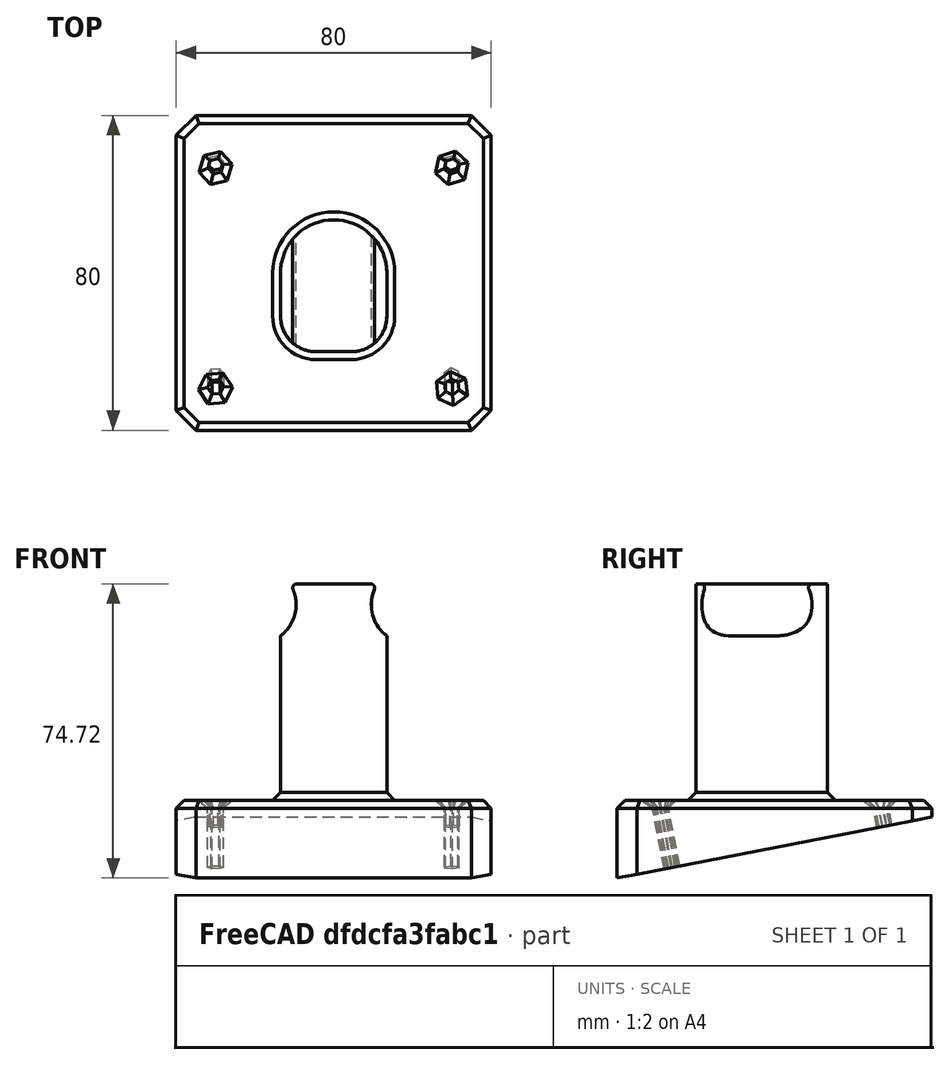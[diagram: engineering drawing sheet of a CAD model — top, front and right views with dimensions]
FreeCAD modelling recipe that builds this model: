
FCSTD DOCUMENT  (FreeCAD 0.19R)
Label: ryobiholder.stl
License: All rights reserved
LicenseURL: http://en.wikipedia.org/wiki/All_rights_reserved
objects: Sketcher::SketchObject×6, PartDesign::Pocket×3, PartDesign::Pad×2, PartDesign::Fillet×2, PartDesign::Chamfer×2, PartDesign::Body×1, Mesh::Feature×1
note: 25 computed .brp shape members not serialized (recipe doc carries the construction recipe); baked Part::Feature solids carry a one-line shape summary decoded from their .brp

FEATURE [Sketcher::SketchObject] Sketch
  FullyConstrained = true
  MapMode = 5
  Support = -> [XY_Plane]
  sketch-geometry (4):
    g0: LineSegment StartX=-40 StartY=40 StartZ=0 EndX=40 EndY=40 EndZ=0
    g1: LineSegment StartX=40 StartY=40 StartZ=0 EndX=40 EndY=-40 EndZ=0
    g2: LineSegment StartX=40 StartY=-40 StartZ=0 EndX=-40 EndY=-40 EndZ=0
    g3: LineSegment StartX=-40 StartY=-40 StartZ=0 EndX=-40 EndY=40 EndZ=0
  constraints (11):
    c: Coincident(g0,g1)
    c: Coincident(g1,g2)
    c: Coincident(g2,g3)
    c: Coincident(g3,g0)
    c: Horizontal(g0)
    c: Horizontal(g2)
    c: Vertical(g1)
    c: Vertical(g3)
    c: Symmetric(g1,g0,g-1)
    c: Equal(g3,g0)
    c: Distance(g0) = 80
FEATURE [PartDesign::Pad] Pad
  Direction = (1,1,1)
  Length = 20
  Length2 = 100
  Profile = -> Sketch
  Type = 0
FEATURE [Sketcher::SketchObject] Sketch001
  FullyConstrained = true
  MapMode = 5
  Placement = pos=(0,0,20) rot=(0,0,1;0rad)
  Support = -> [Pad]
  sketch-geometry (4):
    g0: LineSegment StartX=-13.5 StartY=-20 StartZ=0 EndX=13.5 EndY=-20 EndZ=0
    g1: LineSegment StartX=13.5 StartY=-20 StartZ=0 EndX=13.5 EndY=0 EndZ=0
    g2: LineSegment StartX=-13.5 StartY=-20 StartZ=0 EndX=-13.5 EndY=0 EndZ=0
    g3: ArcOfCircle CenterX=0 CenterY=0 CenterZ=0 NormalX=0 NormalY=0 NormalZ=1 AngleXU=0 Radius=13.5 StartAngle=0 EndAngle=3.14159
  constraints (12):
    c: Horizontal(g0)
    c: Coincident(g0,g1)
    c: PointOnObject(g1,g-1)
    c: Coincident(g0,g2)
    c: PointOnObject(g2,g-1)
    c: Vertical(g2)
    c: Coincident(g3,g-1)
    c: Coincident(g3,g2)
    c: Coincident(g1,g3)
    c: Vertical(g1)
    c: Distance(g0) = 27
    c: Distance(g1) = 20
FEATURE [PartDesign::Pad] Pad001
  BaseFeature = -> Pad
  Direction = (1,1,1)
  Length = 55
  Length2 = 100
  Profile = -> Sketch001
  Type = 0
FEATURE [Sketcher::SketchObject] Sketch002
  FullyConstrained = false
  MapMode = 5
  Placement = pos=(40,0,0) rot=(0.57735,0.57735,0.57735;2.0944rad)
  Support = -> [Pad001]
  sketch-geometry (3):
    g0: LineSegment StartX=70.0227 StartY=21.5734 StartZ=0 EndX=-64.7482 EndY=-4.51106 EndZ=0
    g1: LineSegment StartX=-64.7482 StartY=-4.51106 StartZ=0 EndX=18.5399 EndY=-74.108 EndZ=0
    g2: LineSegment StartX=18.5399 StartY=-74.108 StartZ=0 EndX=70.0227 EndY=21.5734 EndZ=0
  constraints (3):
    c: Coincident(g0,g1)
    c: Coincident(g1,g2)
    c: Coincident(g2,g0)
FEATURE [PartDesign::Pocket] Pocket
  BaseFeature = -> Pad001
  Length = 5
  Length2 = 100
  Profile = -> Sketch002
  Type = 1
FEATURE [PartDesign::Fillet] Fillet
  Base = -> Pocket [Edge22,Edge17]
  BaseFeature = -> Pocket
  Radius = 9
  SupportTransform = false
FEATURE [PartDesign::Chamfer] Chamfer
  Angle = 45
  Base = -> Fillet [Edge25,Edge27,Edge29,Edge24]
  BaseFeature = -> Fillet
  ChamferType = 0
  FlipDirection = false
  Size = 5
  Size2 = 1
  SupportTransform = false
FEATURE [Sketcher::SketchObject] Sketch003
  FullyConstrained = false
  MapMode = 5
  Placement = pos=(0,-1.49633,7.73113) rot=(1,0,0;3.33277rad)
  Support = -> [Chamfer]
  sketch-geometry (28):
    g0: LineSegment StartX=-29.1405 StartY=23.1941 StartZ=0 EndX=-28.0063 EndY=24.8414 EndZ=0
    g1: LineSegment StartX=-28.0063 StartY=24.8414 StartZ=0 EndX=-28.8658 EndY=26.6473 EndZ=0
    g2: LineSegment StartX=-28.8658 StartY=26.6473 StartZ=0 EndX=-30.8595 EndY=26.8059 EndZ=0
    g3: LineSegment StartX=-30.8595 StartY=26.8059 StartZ=0 EndX=-31.9937 EndY=25.1586 EndZ=0
    g4: LineSegment StartX=-31.9937 StartY=25.1586 StartZ=0 EndX=-31.1342 EndY=23.3527 EndZ=0
    g5: LineSegment StartX=-31.1342 StartY=23.3527 StartZ=0 EndX=-29.1405 EndY=23.1941 EndZ=0
    g6: Circle CenterX=-30 CenterY=25 CenterZ=0 NormalX=0 NormalY=0 NormalZ=1 AngleXU=0 Radius=2
    g7: LineSegment StartX=31.6162 StartY=23.822 StartZ=0 EndX=31.8283 EndY=25.8107 EndZ=0
    g8: LineSegment StartX=31.8283 StartY=25.8107 StartZ=0 EndX=30.2121 EndY=26.9887 EndZ=0
    g9: LineSegment StartX=30.2121 StartY=26.9887 StartZ=0 EndX=28.3838 EndY=26.178 EndZ=0
    g10: LineSegment StartX=28.3838 StartY=26.178 StartZ=0 EndX=28.1717 EndY=24.1893 EndZ=0
    g11: LineSegment StartX=28.1717 StartY=24.1893 StartZ=0 EndX=29.7879 EndY=23.0113 EndZ=0
    g12: LineSegment StartX=29.7879 StartY=23.0113 StartZ=0 EndX=31.6162 EndY=23.822 EndZ=0
    g13: Circle CenterX=30 CenterY=25 CenterZ=0 NormalX=0 NormalY=0 NormalZ=1 AngleXU=0 Radius=2
    g14: LineSegment StartX=-28.0536 StartY=-30.4601 StartZ=0 EndX=-28.6284 EndY=-28.5445 EndZ=0
    g15: LineSegment StartX=-28.6284 StartY=-28.5445 StartZ=0 EndX=-30.5747 EndY=-28.0844 EndZ=0
    g16: LineSegment StartX=-30.5747 StartY=-28.0844 StartZ=0 EndX=-31.9464 EndY=-29.5399 EndZ=0
    g17: LineSegment StartX=-31.9464 StartY=-29.5399 StartZ=0 EndX=-31.3716 EndY=-31.4555 EndZ=0
    g18: LineSegment StartX=-31.3716 StartY=-31.4555 StartZ=0 EndX=-29.4253 EndY=-31.9156 EndZ=0
    g19: LineSegment StartX=-29.4253 StartY=-31.9156 StartZ=0 EndX=-28.0536 EndY=-30.4601 EndZ=0
    g20: Circle CenterX=-30 CenterY=-30 CenterZ=0 NormalX=0 NormalY=0 NormalZ=1 AngleXU=0 Radius=2
    g21: LineSegment StartX=31.906 StartY=-30.606 StartZ=0 EndX=31.4778 EndY=-28.6524 EndZ=0
    g22: LineSegment StartX=31.4778 StartY=-28.6524 StartZ=0 EndX=29.5718 EndY=-28.0464 EndZ=0
    g23: LineSegment StartX=29.5718 StartY=-28.0464 StartZ=0 EndX=28.094 EndY=-29.394 EndZ=0
    g24: LineSegment StartX=28.094 StartY=-29.394 StartZ=0 EndX=28.5222 EndY=-31.3476 EndZ=0
    g25: LineSegment StartX=28.5222 StartY=-31.3476 StartZ=0 EndX=30.4282 EndY=-31.9536 EndZ=0
    g26: LineSegment StartX=30.4282 StartY=-31.9536 StartZ=0 EndX=31.906 EndY=-30.606 EndZ=0
    g27: Circle CenterX=30 CenterY=-30 CenterZ=0 NormalX=0 NormalY=0 NormalZ=1 AngleXU=0 Radius=2
  constraints (62):
    c: Coincident(g0,g1)
    c: Coincident(g1,g2)
    c: Coincident(g2,g3)
    c: Coincident(g3,g4)
    c: Coincident(g4,g5)
    c: Coincident(g5,g0)
    c: Equal(g0, g1-g5) x5
    c: PointOnObject(g0,g6)
    c: PointOnObject(g1,g6)
    c: PointOnObject(g2,g6)
    c: PointOnObject(g3,g6)
    c: PointOnObject(g4,g6)
    c: PointOnObject(g5,g6)
    c: Coincident(g7,g8)
    c: Coincident(g8,g9)
    c: Coincident(g9,g10)
    c: Coincident(g10,g11)
    c: Coincident(g11,g12)
    c: Coincident(g12,g7)
    c: Equal(g7, g8-g12) x5
    c: PointOnObject(g7,g13)
    c: PointOnObject(g8,g13)
    c: PointOnObject(g9,g13)
    c: PointOnObject(g10,g13)
    c: PointOnObject(g11,g13)
    c: PointOnObject(g12,g13)
    c: Coincident(g14,g15)
    c: Coincident(g15,g16)
    c: Coincident(g16,g17)
    c: Coincident(g17,g18)
    c: Coincident(g18,g19)
    c: Coincident(g19,g14)
    c: Equal(g14, g15-g19) x5
    c: PointOnObject(g14,g20)
    c: PointOnObject(g15,g20)
    c: PointOnObject(g16,g20)
    c: PointOnObject(g17,g20)
    c: PointOnObject(g18,g20)
    c: PointOnObject(g19,g20)
    c: Coincident(g21,g22)
    c: Coincident(g22,g23)
    c: Coincident(g23,g24)
    c: Coincident(g24,g25)
    c: Coincident(g25,g26)
    c: Coincident(g26,g21)
    c: Equal(g21, g22-g26) x5
    c: PointOnObject(g21,g27)
    c: PointOnObject(g22,g27)
    c: PointOnObject(g23,g27)
    c: PointOnObject(g24,g27)
    c: PointOnObject(g25,g27)
    c: PointOnObject(g26,g27)
    c: Radius(g27) = 2
    c: Equal(g27,g13)
    c: Equal(g27,g6)
    c: Equal(g27,g20)
    c: Symmetric(g13,g6,g-2)
    c: Symmetric(g27,g20,g-2)
    c: DistanceX(g27) = 30
    c: DistanceX(g13) = 30
    c: DistanceY(g13) = 25
    c: DistanceY(g27) = -30
FEATURE [PartDesign::Pocket] Pocket001
  BaseFeature = -> Chamfer
  Length = 5
  Length2 = 100
  Profile = -> Sketch003
  Type = 1
FEATURE [PartDesign::Chamfer] Chamfer001
  Angle = 45
  Base = -> Pocket001 [Face1]
  BaseFeature = -> Pocket001
  ChamferType = 0
  FlipDirection = false
  Size = 2
  Size2 = 1
  SupportTransform = false
FEATURE [Sketcher::SketchObject] Sketch004
  FullyConstrained = false
  MapMode = 5
  Placement = pos=(0,0,0) rot=(0.57735,0.57735,0.57735;2.0944rad)
  Support = -> [YZ_Plane]
  sketch-geometry (1):
    g0: Circle CenterX=-23.5631 CenterY=67.9348 CenterZ=0 NormalX=0 NormalY=0 NormalZ=1 AngleXU=0 Radius=4.98686
FEATURE [Sketcher::SketchObject] Sketch005
  FullyConstrained = false
  MapMode = 5
  Placement = pos=(0,0,0) rot=(1,0,0;1.5708rad)
  Support = -> [XZ_Plane]
  sketch-geometry (2):
    g0: Circle CenterX=19.5483 CenterY=69.7457 CenterZ=0 NormalX=0 NormalY=0 NormalZ=1 AngleXU=0 Radius=10
    g1: Circle CenterX=-19.5483 CenterY=69.7457 CenterZ=0 NormalX=0 NormalY=0 NormalZ=1 AngleXU=0 Radius=10
  constraints (3):
    c: Symmetric(g1,g0,g-2)
    c: Radius(g0) = 10
    c: Equal(g0,g1)
FEATURE [PartDesign::Pocket] Pocket002
  BaseFeature = -> Chamfer001
  Length = 5
  Length2 = 100
  Midplane = true
  Profile = -> Sketch005
  Type = 1
FEATURE [PartDesign::Fillet] Fillet001
  Base = -> Pocket002 [Edge223,Edge222]
  BaseFeature = -> Pocket002
  Radius = 1
  SupportTransform = false
FEATURE [PartDesign::Body] Body
  Group = -> [Sketch,Pad,Sketch001,Pad001,Sketch002,Pocket,Fillet,Chamfer,Sketch003,Pocket001,Chamfer001,Sketch004,Sketch005,Pocket002,Fillet001]
  Origin = -> Origin
  Tip = -> Fillet001
FEATURE [Mesh::Feature] Mesh  label="Fillet001 (Meshed)"
